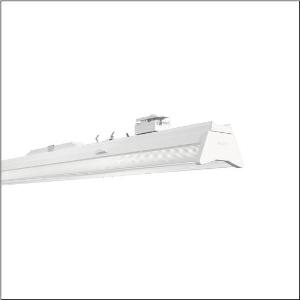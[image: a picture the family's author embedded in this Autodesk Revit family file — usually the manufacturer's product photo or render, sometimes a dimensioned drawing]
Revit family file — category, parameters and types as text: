
# Revit family: licross_r__11_performance_ho_51tm16cn4exm_9d3d
name_source: partatom
category: Lighting Fixtures
units: mm (PartAtom-declared; Revit-internal decimal feet)

## family parameters
Cut with Voids When Loaded = No
Host = Face
Light Source = No
Part Type = Normal
Room Calculation Point = No
Round Connector Dimension = Use Diameter
Shared = No

## types (1)
- --- (1 x LED, 14420 lm, 77.6 W, 4000K)
    Apparent Load = 78 VA
    CIE Flux Codes = 63 87 95 78 100
    Color Rendering = 80
    Color Temperature = 4000K
    Default Elevation = 1800 mm
    Description = Licross® 11 Performance HO, luminaire insert, of sheet steel, galvanised, coil coated, white, length: 1.500mm, width: 120mm, height: 123mm, LED rated luminous flux: 14.420lm, light colour: 840, control gear: ON/OFF Multilumen, CLOi, with plug, 3-pole, with phase selection, mains connection: 220..240V, AC, 50/60Hz, start of lifetime: 78W, end of service life: 87W, halogen-free wiring, primary light control with lens, of plastic, primary optical cover: cover, of PMMA, light emission: direct/indirect distribution, primary light characteristic: symmetric, protection rating (complete): IP40, insulation class (complete): insulation class I (protective earthing), certification: CE, ENEC, VDE, UKCA, protection symbol: D if used in an environment without relevant dust loads with corresponding accessories, impact resistance: IK06, permissible ambient temperature for indoor applications: -35..+35°C, corresponds to IFS (International Featured Standards) requirements for safety and quality in the food industry, reducing of maximum allowable ambient temperature of 5°C with ceiling mounting, LABS conformity tested according to VDMA 24364:2018-05, packaging unit: 1 piece
    Height = 114 mm
    Lamp = 1 x LED
    Lamp Light Flux = 14420 lm
    Lamp Power = 77.6 W
    Lamp count = 1
    Length = 1500 mm
    Luminous efficacy = 186 lm/W
    Manufacturer = Siteco
    ModVariant = No
    Model = 51TM16CN4EXM
    Mounting Place = Ceiling
    Mounting Type = Pendant
    Number of Poles = 1
    OnlyDefault = Yes
    Power Factor = 1
    Product Name = Licross® 11 Performance HO
    Product group = luminaire insert
    ProductGroupID = 901
    Protection Class = Protection class I
    Protection Degree = IP 40
    RLX_Detail_Level = 1
    RLX_Emergency_Light_Flux = 0 lm
    RLX_Emergency_Type = 0
    RLX_Emergency_Type_DB = No
    RlxData = <blob elided: 31817 chars, md5=93b7f0ee>
    Socket = socket
    Standby Power = 0 W
    System Light Flux = 14420 lm
    System Power = 78 W
    Type Comments = factory setting: luminous flux: 100 % | (A | C | E) | 181 mA
    Type Image = l_1256138.jpg
    URL = http://relux.com
    VarID = @adj_055517
    Voltage = 0 V
    Weight = 0.00 kg
    Width = 120 mm

## geometry (parser evidence)
native form markers: Blend x4, Sweep x12
no freeform markers — native parametric forms only
